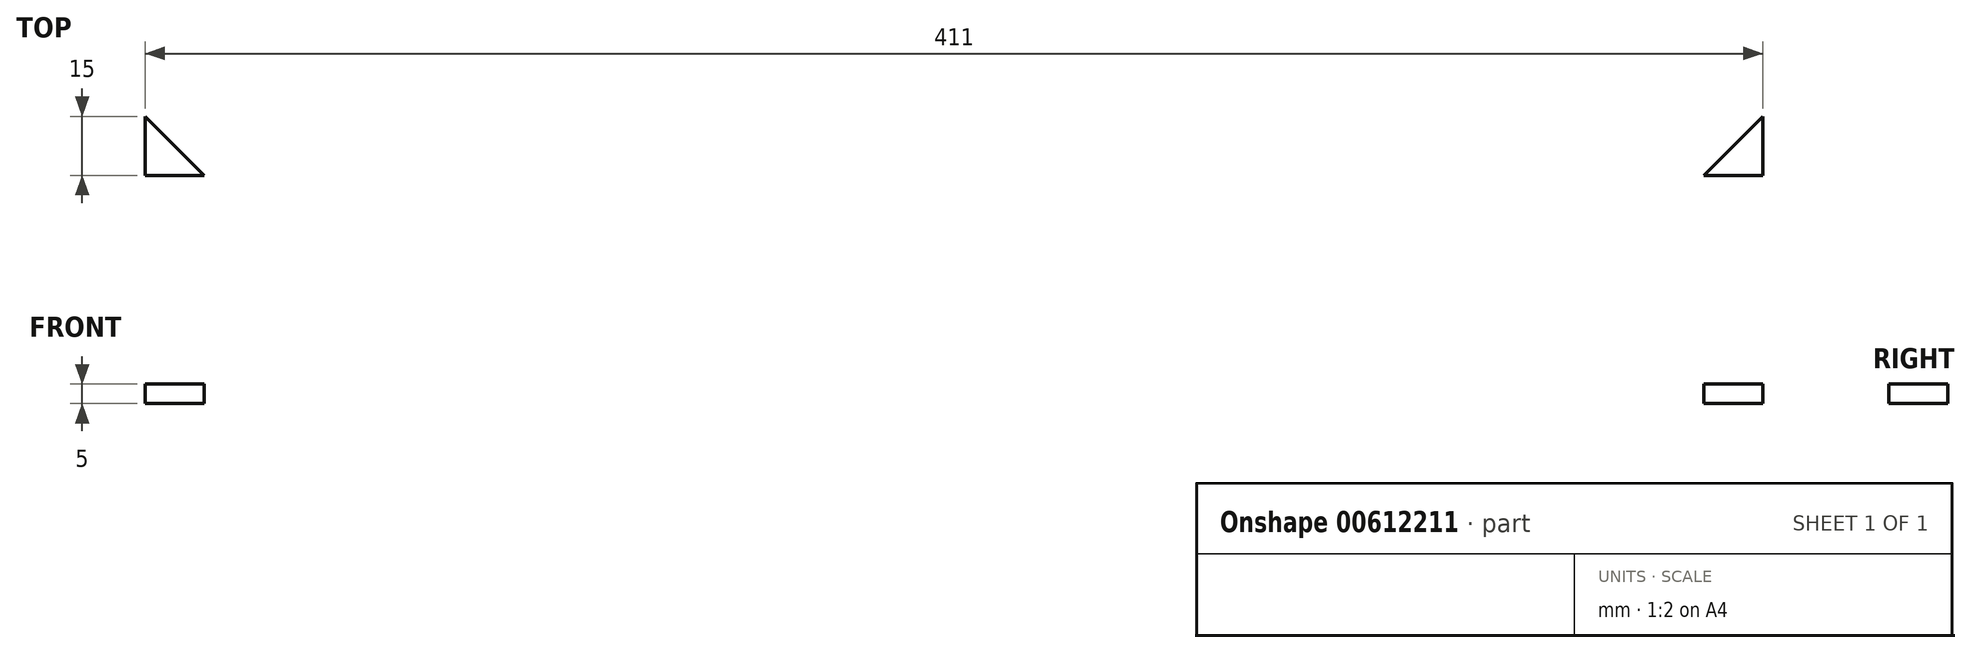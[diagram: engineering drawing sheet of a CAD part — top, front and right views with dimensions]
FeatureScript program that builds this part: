
annotation { "Feature Type Name" : "Feature", "Feature Type Description" : "" }
export const myFeature = defineFeature(function(context is Context, id is Id, definition is map)
    precondition{}
    {
        {
            var Q0;
            Q0=qCreatedBy(makeId("Top.planeOp"),FACE);
            var sketch = newSketch(context, id + "F0", { "sketchPlane" : qUnion([Q0])});
            skLineSegment(sketch, "E0.bottom", {"start": v(-21.93, 0) * mm, "end": v(389.07, 0) * mm});
            skLineSegment(sketch, "E0.top", {"start": v(-21.93, 350) * mm, "end": v(389.07, 350) * mm});
            skLineSegment(sketch, "E0.left", {"start": v(-21.93, 0) * mm, "end": v(-21.93, 350) * mm});
            skLineSegment(sketch, "E0.right", {"start": v(389.07, 0) * mm, "end": v(389.07, 350) * mm});
            skLineSegment(sketch, "E1", {"start": v(-21.93, 15) * mm, "end": v(-6.93, 0) * mm});
            skLineSegment(sketch, "E2", {"start": v(-21.93, 335) * mm, "end": v(-6.93, 350) * mm});
            skLineSegment(sketch, "E3", {"start": v(374.07, 350) * mm, "end": v(389.07, 335) * mm});
            skLineSegment(sketch, "E4", {"start": v(374.07, 0) * mm, "end": v(389.07, 15) * mm});
            skLineSegment(sketch, "E5", {"start": v(-21.93, 0) * mm, "end": v(-6.93, 0) * mm});
            skLineSegment(sketch, "E6", {"start": v(-21.93, 0) * mm, "end": v(-21.93, 15) * mm});
            skLineSegment(sketch, "E7", {"start": v(-21.93, 335) * mm, "end": v(-21.93, 350) * mm});
            skLineSegment(sketch, "E8", {"start": v(-6.93, 350) * mm, "end": v(-21.93, 350) * mm});
            skLineSegment(sketch, "E9", {"start": v(374.07, 350) * mm, "end": v(389.07, 350) * mm});
            skLineSegment(sketch, "E10", {"start": v(389.07, 335) * mm, "end": v(389.07, 350) * mm});
            skLineSegment(sketch, "E11", {"start": v(389.07, 0) * mm, "end": v(389.07, 15) * mm});
            skLineSegment(sketch, "E12", {"start": v(374.07, 0) * mm, "end": v(389.07, 0) * mm});
            skLineSegment(sketch, "E13", {"start": v(389.07, 15) * mm, "end": v(389.07, 0) * mm});
            skLineSegment(sketch, "E14", {"start": v(389.07, 0) * mm, "end": v(374.07, 0) * mm});
            skSolve(sketch);
        }
        {
            var Q0;
            Q0=makeQuery(id+"F0.imprint","IMPRINT",FACE,{"disambiguationData":[TD([[makeQuery(id+"F0.imprint","IMPRINT",EDGE,{"derivedFrom":sQuery(id+"F0.wireOp",EDGE,"E0.bottom")}),1.0]])]});
            extrude(context, id + "F1", {"entities" : qUnion([Q0]), "depth" : 5 * mm});
        }
    });
